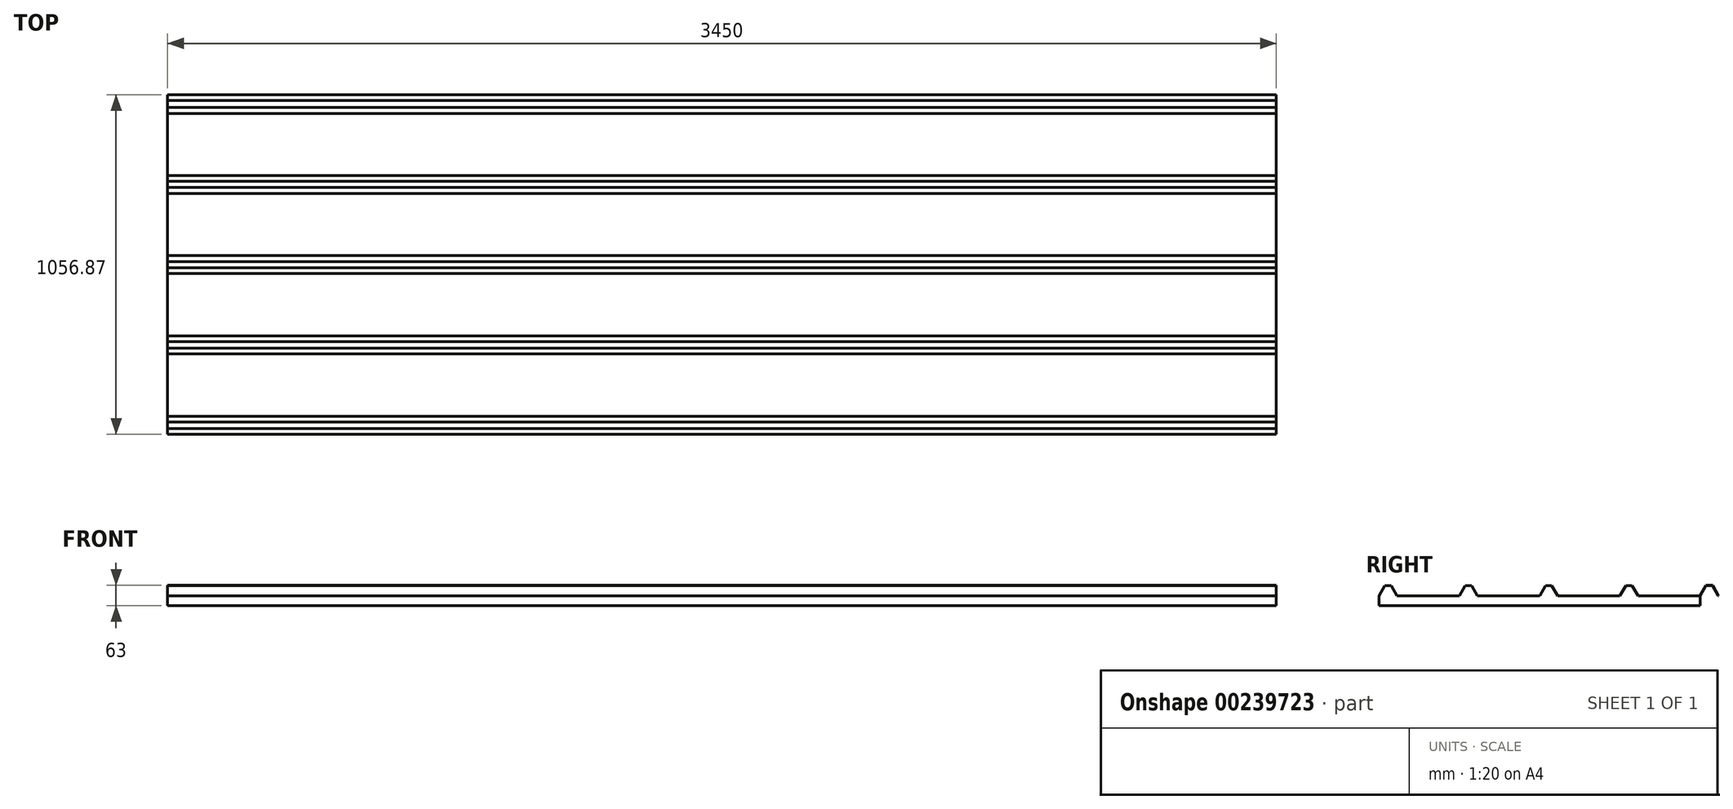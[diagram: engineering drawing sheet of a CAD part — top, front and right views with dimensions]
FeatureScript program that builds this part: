
annotation { "Feature Type Name" : "Feature", "Feature Type Description" : "" }
export const myFeature = defineFeature(function(context is Context, id is Id, definition is map)
    precondition{}
    {
        {
            var Q0;
            Q0=qCreatedBy(makeId("Top.planeOp"),FACE);
            var sketch = newSketch(context, id + "F0", { "sketchPlane" : qUnion([Q0])});
            skLineSegment(sketch, "E0.bottom", {"start": v(0, 0) * mm, "end": v(3450, 0) * mm});
            skLineSegment(sketch, "E0.top", {"start": v(0, 1000) * mm, "end": v(3450, 1000) * mm});
            skLineSegment(sketch, "E0.left", {"start": v(0, 0) * mm, "end": v(0, 1000) * mm});
            skLineSegment(sketch, "E0.right", {"start": v(3450, 0) * mm, "end": v(3450, 1000) * mm});
            skSolve(sketch);
        }
        {
            var Q0;
            Q0=makeQuery(id+"F0.imprint","IMPRINT",FACE,{"disambiguationData":[TD([[makeQuery(id+"F0.imprint","IMPRINT",EDGE,{"derivedFrom":sQuery(id+"F0.wireOp",EDGE,"E0.bottom")}),1.0]])]});
            extrude(context, id + "F1", {"entities" : qUnion([Q0]), "depth" : 30 * mm});
        }
        {
            var Q0;
            Q0=makeQuery(id+"F1.opExtrude","SWEPT_FACE",FACE,{"disambiguationData":[OSD([sQuery(id+"F0.wireOp",EDGE,"E0.right")])]});
            var sketch = newSketch(context, id + "F2", { "sketchPlane" : qUnion([Q0])});
            skLineSegment(sketch, "E1", {"start": v(0, 30) * mm, "end": v(18, 62) * mm});
            skLineSegment(sketch, "E2", {"start": v(18, 62) * mm, "end": v(38, 62) * mm});
            skLineSegment(sketch, "E3", {"start": v(38, 62) * mm, "end": v(56, 30) * mm});
            skLineSegment(sketch, "E4.1.0.0", {"start": v(250, 30) * mm, "end": v(268, 62) * mm});
            skLineSegment(sketch, "E4.1.0.1", {"start": v(268, 62) * mm, "end": v(288, 62) * mm});
            skLineSegment(sketch, "E4.1.0.2", {"start": v(288, 62) * mm, "end": v(306, 30) * mm});
            skLineSegment(sketch, "E4.2.0.0", {"start": v(500, 30) * mm, "end": v(518, 62) * mm});
            skLineSegment(sketch, "E4.2.0.1", {"start": v(518, 62) * mm, "end": v(538, 62) * mm});
            skLineSegment(sketch, "E4.2.0.2", {"start": v(538, 62) * mm, "end": v(556, 30) * mm});
            skLineSegment(sketch, "E4.3.0.0", {"start": v(750, 30) * mm, "end": v(768, 62) * mm});
            skLineSegment(sketch, "E4.3.0.1", {"start": v(768, 62) * mm, "end": v(788, 62) * mm});
            skLineSegment(sketch, "E4.3.0.2", {"start": v(788, 62) * mm, "end": v(806, 30) * mm});
            skLineSegment(sketch, "E4.4.0.0", {"start": v(1000, 30) * mm, "end": v(1018, 62) * mm});
            skLineSegment(sketch, "E4.4.0.1", {"start": v(1018, 62) * mm, "end": v(1038, 62) * mm});
            skLineSegment(sketch, "E4.4.0.2", {"start": v(1038, 62) * mm, "end": v(1056, 30) * mm});
            skLineSegment(sketch, "E4.direction1", {"start": v(0, 30) * mm, "end": v(250, 30) * mm, "construction": true});
            skLineSegment(sketch, "E5.0", {"start": v(1038.58, 63) * mm, "end": v(1056.87, 30.5) * mm});
            skLineSegment(sketch, "E5.1", {"start": v(1017.42, 63) * mm, "end": v(1038.58, 63) * mm});
            skLineSegment(sketch, "E5.2", {"start": v(998.85, 30) * mm, "end": v(1017.42, 63) * mm});
            skLineSegment(sketch, "E6", {"start": v(1056.87, 30.5) * mm, "end": v(1056, 30) * mm});
            skSolve(sketch);
        }
        {
            var Q0;
            Q0 = qSketchRegion(id + "F2", true);
            var Q1;
            {var subQ0=sQuery(id+"F2.wireOp",EDGE,"E1");Q1=makeQuery(id+"F2.imprint","IMPRINT",FACE,{"disambiguationData":[TD([[makeQuery(id+"F2.imprint","IMPRINT",EDGE,{"derivedFrom":subQ0}),-1.0]])]});}
            var Q2;
            {var subQ0=sQuery(id+"F2.wireOp",EDGE,"E4.1.0.0");Q2=makeQuery(id+"F2.imprint","IMPRINT",FACE,{"disambiguationData":[TD([[makeQuery(id+"F2.imprint","IMPRINT",EDGE,{"derivedFrom":subQ0}),-1.0]])]});}
            var Q3;
            {var subQ0=sQuery(id+"F2.wireOp",EDGE,"E4.2.0.0");Q3=makeQuery(id+"F2.imprint","IMPRINT",FACE,{"disambiguationData":[TD([[makeQuery(id+"F2.imprint","IMPRINT",EDGE,{"derivedFrom":subQ0}),-1.0]])]});}
            var Q4;
            {var subQ0=sQuery(id+"F2.wireOp",EDGE,"E4.3.0.0");Q4=makeQuery(id+"F2.imprint","IMPRINT",FACE,{"disambiguationData":[TD([[makeQuery(id+"F2.imprint","IMPRINT",EDGE,{"derivedFrom":subQ0}),-1.0]])]});}
            var Q5;
            {var subQ0=sQuery(id+"F2.wireOp",EDGE,"E4.4.0.0");Q5=makeQuery(id+"F2.imprint","IMPRINT",FACE,{"disambiguationData":[TD([[makeQuery(id+"F2.imprint","IMPRINT",EDGE,{"derivedFrom":subQ0}),1.0]])]});}
            extrude(context, id + "F3", {"entities" : qUnion([Q0, Q1, Q2, Q3, Q4, Q5]), "operationType" : NewBodyOperationType.ADD, "oppositeDirection" : true, "depth" : 3450 * mm});
        }
    });
